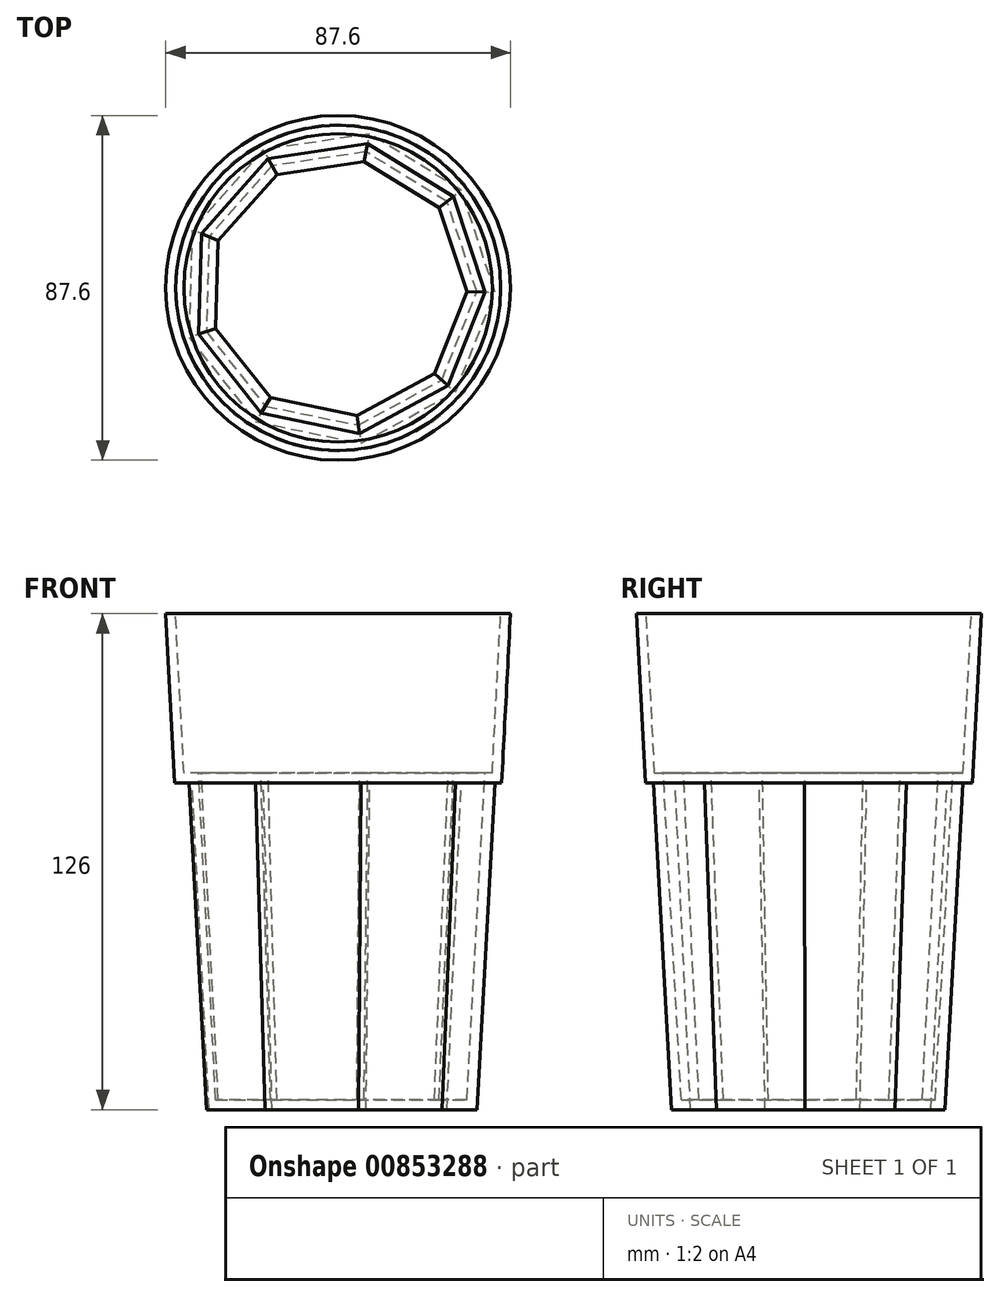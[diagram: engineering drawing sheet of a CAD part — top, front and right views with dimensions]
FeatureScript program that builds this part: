
annotation { "Feature Type Name" : "Feature", "Feature Type Description" : "" }
export const myFeature = defineFeature(function(context is Context, id is Id, definition is map)
    precondition{}
    {
        {
            var Q0;
            Q0=qCreatedBy(makeId("Top.planeOp"),FACE);
            var sketch = newSketch(context, id + "F0", { "sketchPlane" : qUnion([Q0])});
            skCircle(sketch, "E0.cCircle", {"center": v(0, 0) * mm, "radius": 37.5 * mm, "construction": true});
            skLineSegment(sketch, "E0.0", {"start": v(39.9, -1.13) * mm, "end": v(29.83, -26.5) * mm});
            skLineSegment(sketch, "E0.1", {"start": v(29.83, -26.5) * mm, "end": v(5.82, -39.48) * mm});
            skLineSegment(sketch, "E0.2", {"start": v(5.82, -39.48) * mm, "end": v(-20.92, -33.98) * mm});
            skLineSegment(sketch, "E0.3", {"start": v(-20.92, -33.98) * mm, "end": v(-37.87, -12.59) * mm});
            skLineSegment(sketch, "E0.4", {"start": v(-37.87, -12.59) * mm, "end": v(-37.1, 14.7) * mm});
            skLineSegment(sketch, "E0.5", {"start": v(-37.1, 14.7) * mm, "end": v(-18.97, 35.1) * mm});
            skLineSegment(sketch, "E0.6", {"start": v(-18.97, 35.1) * mm, "end": v(8.04, 39.09) * mm});
            skLineSegment(sketch, "E0.7", {"start": v(8.04, 39.09) * mm, "end": v(31.28, 24.78) * mm});
            skLineSegment(sketch, "E0.8", {"start": v(31.28, 24.78) * mm, "end": v(39.9, -1.13) * mm});
            skPoint(sketch, "E0.0.midPoint", {"position": v(34.86, -13.82) * mm});
            skCircle(sketch, "E1", {"center": v(0, 0) * mm, "radius": 41.57 * mm});
            skSolve(sketch);
        }
        {
            var Q0;
            Q0=makeQuery(id+"F0.imprint","IMPRINT",FACE,{"disambiguationData":[TD([[makeQuery(id+"F0.imprint","IMPRINT",EDGE,{"derivedFrom":sQuery(id+"F0.wireOp",EDGE,"E0.0")}),-1.0]])]});
            extrude(context, id + "F1", {"entities" : qUnion([Q0]), "oppositeDirection" : true, "depth" : 83 * mm, "offsetDistance" : 25 * mm, "hasDraft" : true, "draftAngle" : 3 * degree, "draftPullDirection" : true});
        }
        {
            var Q0;
            Q0=qCreatedBy(makeId("Top.planeOp"),FACE);
            var sketch = newSketch(context, id + "F2", { "sketchPlane" : qUnion([Q0])});
            skCircle(sketch, "E2", {"center": v(0, 0) * mm, "radius": 41.54 * mm});
            skSolve(sketch);
        }
        {
            var Q0;
            Q0 = qSketchRegion(id + "F2", true);
            extrude(context, id + "F3", {"entities" : qUnion([Q0]), "operationType" : NewBodyOperationType.ADD, "depth" : 43 * mm, "offsetDistance" : 25 * mm, "hasDraft" : true, "draftAngle" : 3 * degree});
        }
        {
            var Q0;
            Q0=makeQuery(id+"F3.opExtrude","CAP_FACE",FACE,{"disambiguationData":[OSD([sQuery(id+"F2.wireOp",EDGE,"E2")])],"isStart":false});
            shell(context, id + "F4", {"entities" : qUnion([Q0]), "thickness" : 2.5 * mm});
        }
    });
